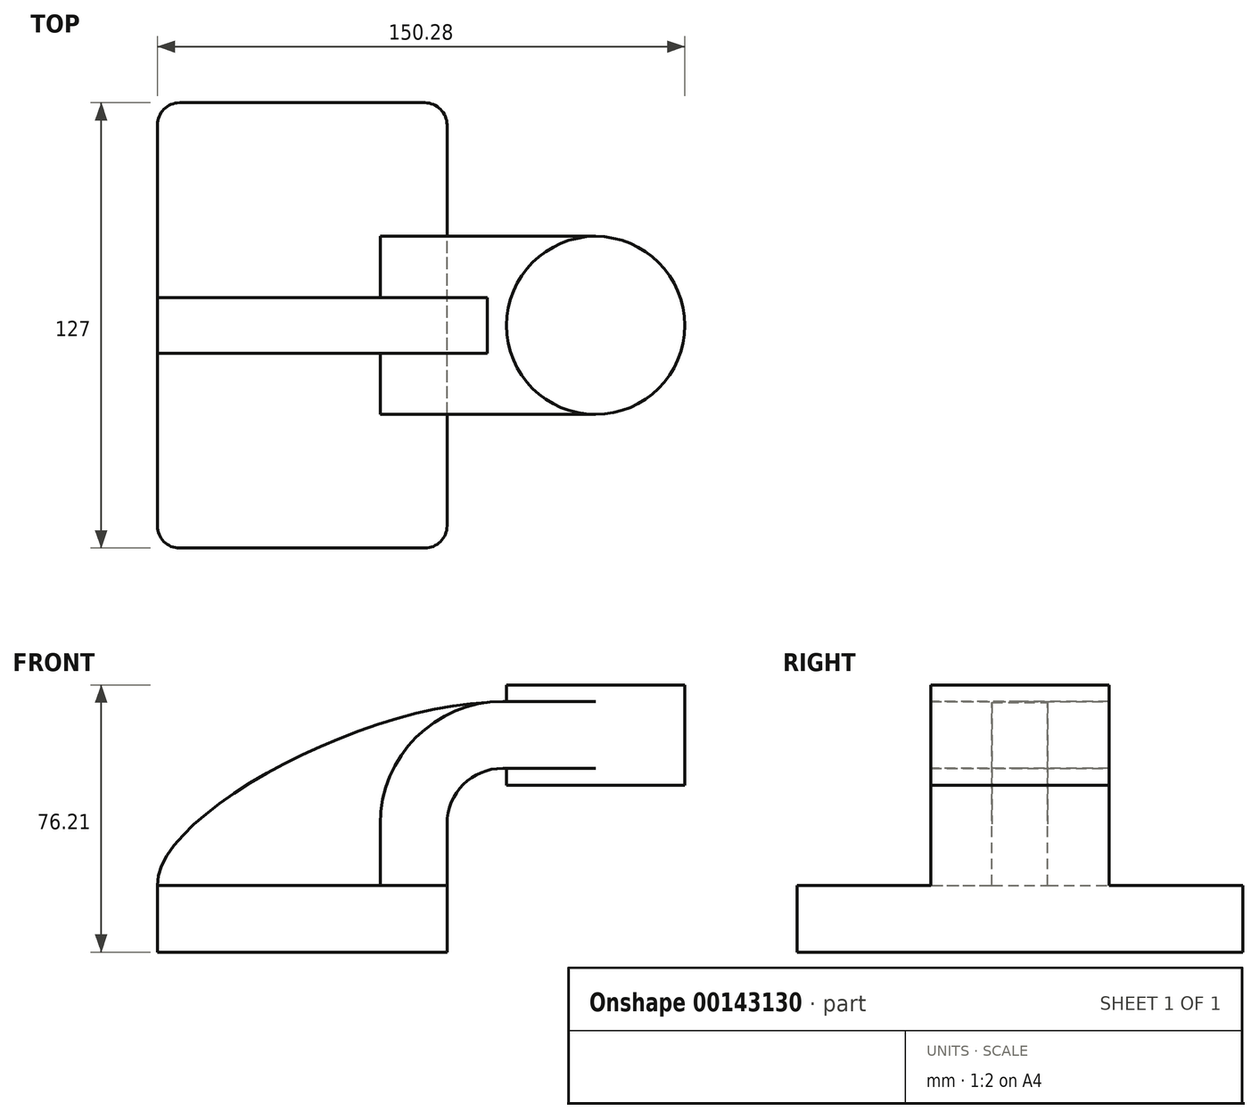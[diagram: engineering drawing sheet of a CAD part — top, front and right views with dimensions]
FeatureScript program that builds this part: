
annotation { "Feature Type Name" : "Feature", "Feature Type Description" : "" }
export const myFeature = defineFeature(function(context is Context, id is Id, definition is map)
    precondition{}
    {
        {
            var Q0;
            Q0=qCreatedBy(makeId("Front.planeOp"),FACE);
            var sketch = newSketch(context, id + "F0", { "sketchPlane" : qUnion([Q0])});
            skLineSegment(sketch, "E0.bottom", {"start": v(-41.28, -9.53) * mm, "end": v(41.28, -9.53) * mm});
            skLineSegment(sketch, "E0.top", {"start": v(-41.28, 9.53) * mm, "end": v(41.28, 9.53) * mm});
            skLineSegment(sketch, "E0.left", {"start": v(-41.28, -9.53) * mm, "end": v(-41.28, 9.53) * mm});
            skLineSegment(sketch, "E0.right", {"start": v(41.28, -9.53) * mm, "end": v(41.28, 9.53) * mm});
            skPoint(sketch, "E0.middle", {"position": v(0, 0) * mm});
            skLineSegment(sketch, "E1.bottom", {"start": v(58.2, 66.67) * mm, "end": v(109, 66.67) * mm});
            skLineSegment(sketch, "E1.top", {"start": v(58.2, 38.1) * mm, "end": v(109, 38.1) * mm});
            skLineSegment(sketch, "E1.left", {"start": v(58.2, 66.67) * mm, "end": v(58.2, 38.1) * mm});
            skLineSegment(sketch, "E1.right", {"start": v(109, 66.67) * mm, "end": v(109, 38.1) * mm});
            skPoint(sketch, "E1.middle", {"position": v(83.6, 52.39) * mm});
            skLineSegment(sketch, "E2", {"start": v(41.28, 9.53) * mm, "end": v(41.28, 27) * mm});
            skArc(sketch, "E3", {"start": v(41.28, 27) * mm, "mid": v(45.92, 38.23) * mm, "end": v(57.15, 42.88) * mm});
            skLineSegment(sketch, "E4", {"start": v(57.15, 42.88) * mm, "end": v(83.6, 42.88) * mm});
            skLineSegment(sketch, "E5.0", {"start": v(57.15, 61.93) * mm, "end": v(83.6, 61.93) * mm});
            skArc(sketch, "E5.1", {"start": v(22.23, 27) * mm, "mid": v(32.45, 51.7) * mm, "end": v(57.15, 61.93) * mm});
            skLineSegment(sketch, "E5.2", {"start": v(22.23, 9.53) * mm, "end": v(22.23, 27) * mm});
            skFitSpline(sketch, "E6", {"points": [v(-41.28, 9.53) * mm, v(52.72, 61.65) * mm], "startDerivative": vector(-0.71, 61.17) * mm, "endDerivative": vector(106.7, 3.66) * mm});
            skLineSegment(sketch, "E7", {"start": v(83.6, 38.1) * mm, "end": v(83.6, 66.67) * mm});
            skSolve(sketch);
        }
        {
            var Q0;
            Q0=makeQuery(id+"F0.imprint","IMPRINT",FACE,{"disambiguationData":[TD([[makeQuery(id+"F0.imprint","IMPRINT",EDGE,{"derivedFrom":sQuery(id+"F0.wireOp",EDGE,"E0.bottom")}),1.0]])]});
            extrude(context, id + "F1", {"entities" : qUnion([Q0]), "endBound" : BoundingType.SYMMETRIC, "depth" : 127 * mm});
        }
        {
            var Q0;
            {var subQ1=sQuery(id+"F0.wireOp",EDGE,"E2");Q0=makeQuery(id+"F0.imprint","IMPRINT",FACE,{"disambiguationData":[TD([[makeQuery(id+"F0.imprint","IMPRINT",EDGE,{"derivedFrom":subQ1}),1.0]])]});}
            var Q1;
            {var subQ0=sQuery(id+"F0.wireOp",EDGE,"E5.0");var subQ1=sQuery(id+"F0.wireOp",EDGE,"E1.left");var subQ2=makeQuery(id+"F0.imprint","INTERSECT",VERTEX,{"derivedFrom":[subQ1,subQ0]});Q1=makeQuery(id+"F0.imprint","IMPRINT",FACE,{"disambiguationData":[TD([[makeQuery(id+"F0.imprint","IMPRINT",EDGE,{"disambiguationData":[TD([[subQ2,-1.0]])],"derivedFrom":subQ1}),1.0]])]});}
            extrude(context, id + "F2", {"entities" : qUnion([Q0, Q1]), "operationType" : NewBodyOperationType.ADD, "endBound" : BoundingType.SYMMETRIC, "depth" : 50.8 * mm});
        }
        {
            var Q0;
            {var subQ2=sQuery(id+"F0.wireOp",EDGE,"E5.2");Q0=makeQuery(id+"F0.imprint","IMPRINT",FACE,{"disambiguationData":[TD([[makeQuery(id+"F0.imprint","IMPRINT",EDGE,{"derivedFrom":subQ2}),1.0]])]});}
            extrude(context, id + "F3", {"entities" : qUnion([Q0]), "operationType" : NewBodyOperationType.ADD, "endBound" : BoundingType.SYMMETRIC, "depth" : 15.88 * mm});
        }
        {
            var Q0;
            {var subQ4=sQuery(id+"F0.wireOp",EDGE,"E1.right");Q0=makeQuery(id+"F0.imprint","IMPRINT",FACE,{"disambiguationData":[TD([[makeQuery(id+"F0.imprint","IMPRINT",EDGE,{"derivedFrom":subQ4}),-1.0]])]});}
            var Q1;
            Q1=sQuery(id+"F0.wireOp",EDGE,"E7");
            revolve(context, id + "F4", {"operationType" : NewBodyOperationType.ADD, "entities" : qUnion([Q0]), "axis" : qUnion([Q1]), "revolveType" : RevolveType.FULL});
        }
        {
            var Q0;
            Q0=makeQuery(id+"F1.opExtrude","CAP_EDGE",EDGE,{"disambiguationData":[OSD([sQuery(id+"F0.wireOp",EDGE,"E0.right")])],"isStart":false});
            var Q1;
            Q1=makeQuery(id+"F1.opExtrude","CAP_EDGE",EDGE,{"disambiguationData":[OSD([sQuery(id+"F0.wireOp",EDGE,"E0.left")])],"isStart":false});
            var Q2;
            Q2=makeQuery(id+"F1.opExtrude","CAP_EDGE",EDGE,{"disambiguationData":[OSD([sQuery(id+"F0.wireOp",EDGE,"E0.right")])],"isStart":true});
            var Q3;
            Q3=makeQuery(id+"F1.opExtrude","CAP_EDGE",EDGE,{"disambiguationData":[OSD([sQuery(id+"F0.wireOp",EDGE,"E0.left")])],"isStart":true});
            fillet(context, id + "F5", {"entities" : qUnion([Q0, Q1, Q2, Q3]), "radius" : 6.35 * mm, "tangentPropagation" : true, "allowEdgeOverflow" : false});
        }
    });
